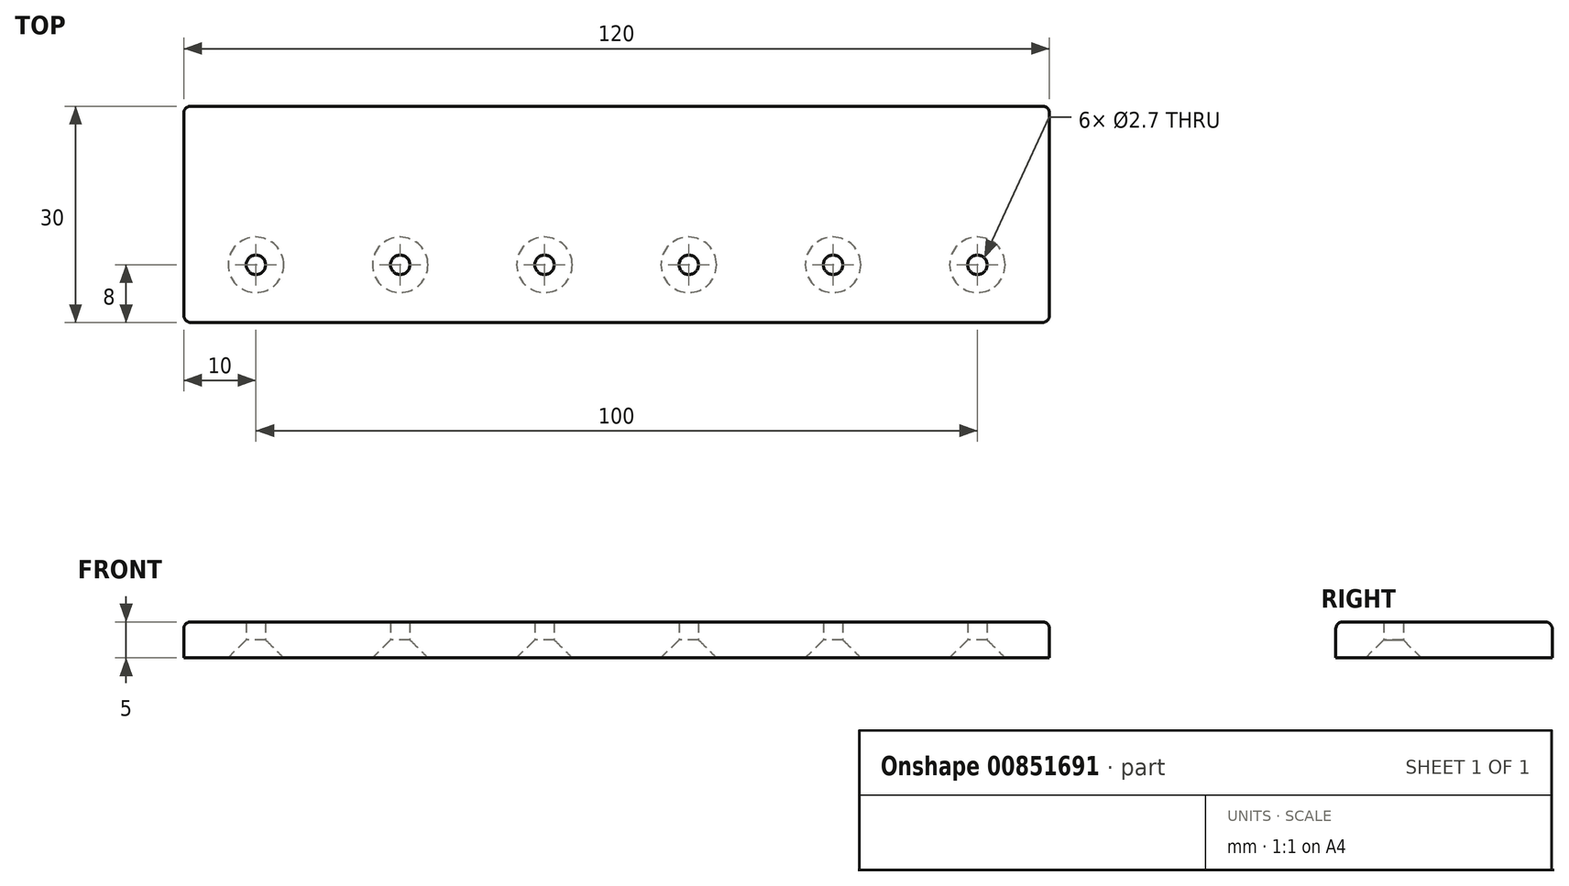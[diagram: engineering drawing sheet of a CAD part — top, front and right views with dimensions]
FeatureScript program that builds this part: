
annotation { "Feature Type Name" : "Feature", "Feature Type Description" : "" }
export const myFeature = defineFeature(function(context is Context, id is Id, definition is map)
    precondition{}
    {
        {
            var Q0;
            Q0=qCreatedBy(makeId("Top.planeOp"),FACE);
            var sketch = newSketch(context, id + "F0", { "sketchPlane" : qUnion([Q0])});
            skLineSegment(sketch, "E0.bottom", {"start": v(-60, 22) * mm, "end": v(60, 22) * mm});
            skLineSegment(sketch, "E0.top", {"start": v(-60, -8) * mm, "end": v(60, -8) * mm});
            skLineSegment(sketch, "E0.left", {"start": v(-60, 22) * mm, "end": v(-60, -8) * mm});
            skLineSegment(sketch, "E0.right", {"start": v(60, 22) * mm, "end": v(60, -8) * mm});
            skCircle(sketch, "E1", {"center": v(-50, 0) * mm, "radius": 1.35 * mm});
            skCircle(sketch, "E2.1.0.0", {"center": v(-30, 0) * mm, "radius": 1.35 * mm});
            skCircle(sketch, "E2.2.0.0", {"center": v(-10, 0) * mm, "radius": 1.35 * mm});
            skCircle(sketch, "E2.3.0.0", {"center": v(10, 0) * mm, "radius": 1.35 * mm});
            skCircle(sketch, "E2.4.0.0", {"center": v(30, 0) * mm, "radius": 1.35 * mm});
            skCircle(sketch, "E2.5.0.0", {"center": v(50, 0) * mm, "radius": 1.35 * mm});
            skLineSegment(sketch, "E2.direction1", {"start": v(-50, 0) * mm, "end": v(-30, 0) * mm, "construction": true});
            skSolve(sketch);
        }
        {
            var Q0;
            Q0 = qSketchRegion(id + "F0", true);
            extrude(context, id + "F1", {"entities" : qUnion([Q0]), "depth" : 5 * mm, "offsetDistance" : 25 * mm});
        }
        {
            var Q0;
            Q0=makeQuery(id+"F1.opExtrude","CAP_EDGE",EDGE,{"disambiguationData":[OSD([sQuery(id+"F0.wireOp",EDGE,"E1")])],"isStart":true});
            var Q1;
            Q1=makeQuery(id+"F1.opExtrude","CAP_EDGE",EDGE,{"disambiguationData":[OSD([sQuery(id+"F0.wireOp",EDGE,"E2.1.0.0")])],"isStart":true});
            var Q2;
            Q2=makeQuery(id+"F1.opExtrude","CAP_EDGE",EDGE,{"disambiguationData":[OSD([sQuery(id+"F0.wireOp",EDGE,"E2.2.0.0")])],"isStart":true});
            var Q3;
            Q3=makeQuery(id+"F1.opExtrude","CAP_EDGE",EDGE,{"disambiguationData":[OSD([sQuery(id+"F0.wireOp",EDGE,"E2.3.0.0")])],"isStart":true});
            var Q4;
            Q4=makeQuery(id+"F1.opExtrude","CAP_EDGE",EDGE,{"disambiguationData":[OSD([sQuery(id+"F0.wireOp",EDGE,"E2.4.0.0")])],"isStart":true});
            var Q5;
            Q5=makeQuery(id+"F1.opExtrude","CAP_EDGE",EDGE,{"disambiguationData":[OSD([sQuery(id+"F0.wireOp",EDGE,"E2.5.0.0")])],"isStart":true});
            chamfer(context, id + "F2", {"entities" : qUnion([Q0, Q1, Q2, Q3, Q4, Q5]), "width" : 2.5 * mm, "tangentPropagation" : true});
        }
        {
            var Q0;
            Q0=makeQuery(id+"F1.opExtrude","CAP_EDGE",EDGE,{"disambiguationData":[OSD([sQuery(id+"F0.wireOp",EDGE,"E0.left")])],"isStart":false});
            var Q1;
            Q1=makeQuery(id+"F1.opExtrude","CAP_EDGE",EDGE,{"disambiguationData":[OSD([sQuery(id+"F0.wireOp",EDGE,"E0.top")])],"isStart":false});
            var Q2;
            Q2=makeQuery(id+"F1.opExtrude","CAP_EDGE",EDGE,{"disambiguationData":[OSD([sQuery(id+"F0.wireOp",EDGE,"E0.right")])],"isStart":false});
            var Q3;
            Q3=makeQuery(id+"F1.opExtrude","CAP_EDGE",EDGE,{"disambiguationData":[OSD([sQuery(id+"F0.wireOp",EDGE,"E0.bottom")])],"isStart":false});
            var Q4;
            Q4=makeQuery(id+"F1.opExtrude","SWEPT_EDGE",EDGE,{"disambiguationData":[OSD([sQuery(id+"F0.wireOp",EDGE,"E0.bottom"),sQuery(id+"F0.wireOp",EDGE,"E0.right")])]});
            var Q5;
            Q5=makeQuery(id+"F1.opExtrude","SWEPT_EDGE",EDGE,{"disambiguationData":[OSD([sQuery(id+"F0.wireOp",EDGE,"E0.top"),sQuery(id+"F0.wireOp",EDGE,"E0.right")])]});
            var Q6;
            Q6=makeQuery(id+"F1.opExtrude","SWEPT_EDGE",EDGE,{"disambiguationData":[OSD([sQuery(id+"F0.wireOp",EDGE,"E0.top"),sQuery(id+"F0.wireOp",EDGE,"E0.left")])]});
            var Q7;
            Q7=makeQuery(id+"F1.opExtrude","SWEPT_EDGE",EDGE,{"disambiguationData":[OSD([sQuery(id+"F0.wireOp",EDGE,"E0.bottom"),sQuery(id+"F0.wireOp",EDGE,"E0.left")])]});
            fillet(context, id + "F3", {"entities" : qUnion([Q0, Q1, Q2, Q3, Q4, Q5, Q6, Q7]), "radius" : 1 * mm, "tangentPropagation" : true, "allowEdgeOverflow" : false});
        }
    });
